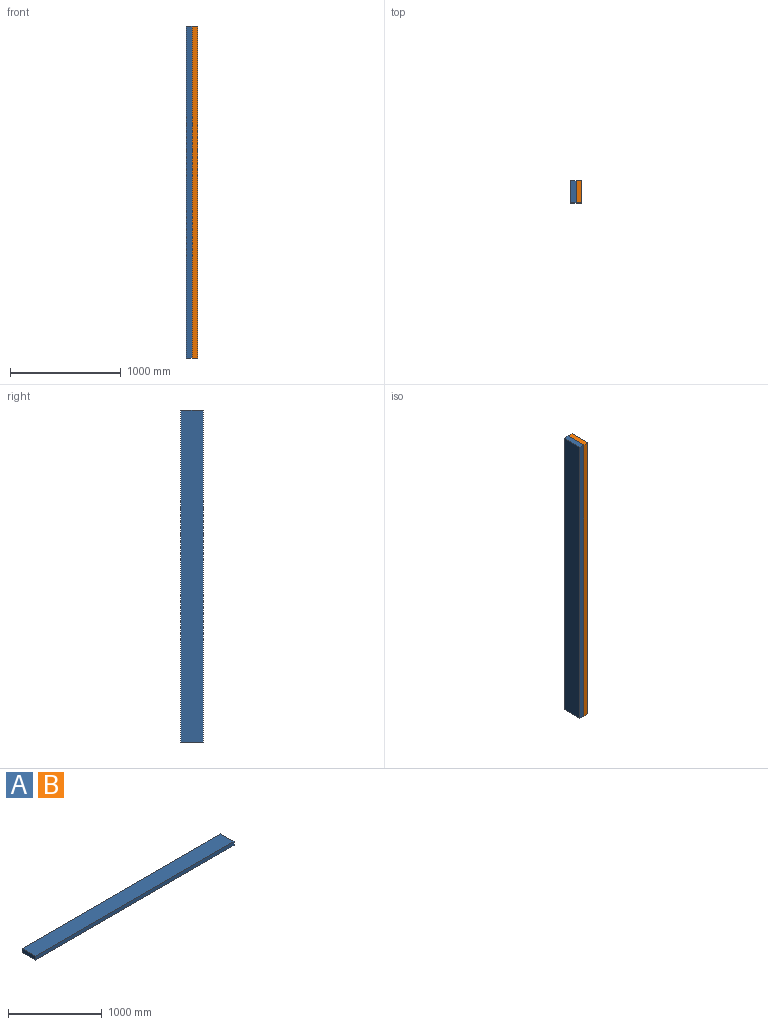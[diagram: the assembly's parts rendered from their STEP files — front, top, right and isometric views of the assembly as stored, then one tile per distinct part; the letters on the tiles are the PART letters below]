
ASSEMBLY  parts=2 mates=1
PART A: 6 faces, bbox 3000x200x50 mm
  f0: plane 3000x50mm, normal (0,1,0), area 150000mm2, adj f1,f3,f4,f5
  f1: plane 200x50mm, normal (-1,0,0), area 10000mm2, adj f0,f2,f4,f5
  f2: plane 3000x50mm, normal (0,-1,0), area 150000mm2, adj f1,f3,f4,f5
  f3: plane 200x50mm, normal (1,0,0), area 10000mm2, adj f0,f2,f4,f5
  f4: plane 3000x200mm, normal (0,0,1), area 600000mm2, adj f0,f1,f2,f3
  f5: plane 3000x200mm, normal (0,0,-1), area 600000mm2, adj f0,f1,f2,f3
PART B: same geometry as A
PLACE A rot(axis=(0,1,0),90deg) t=(-50,0,0)mm
PLACE B rot(axis=(0.71,0,-0.71),180deg) t=(50,0,0)mm
MATE fastened A.f4 <-> B.f4  axis (1,0,0) through (0,0,0)mm
